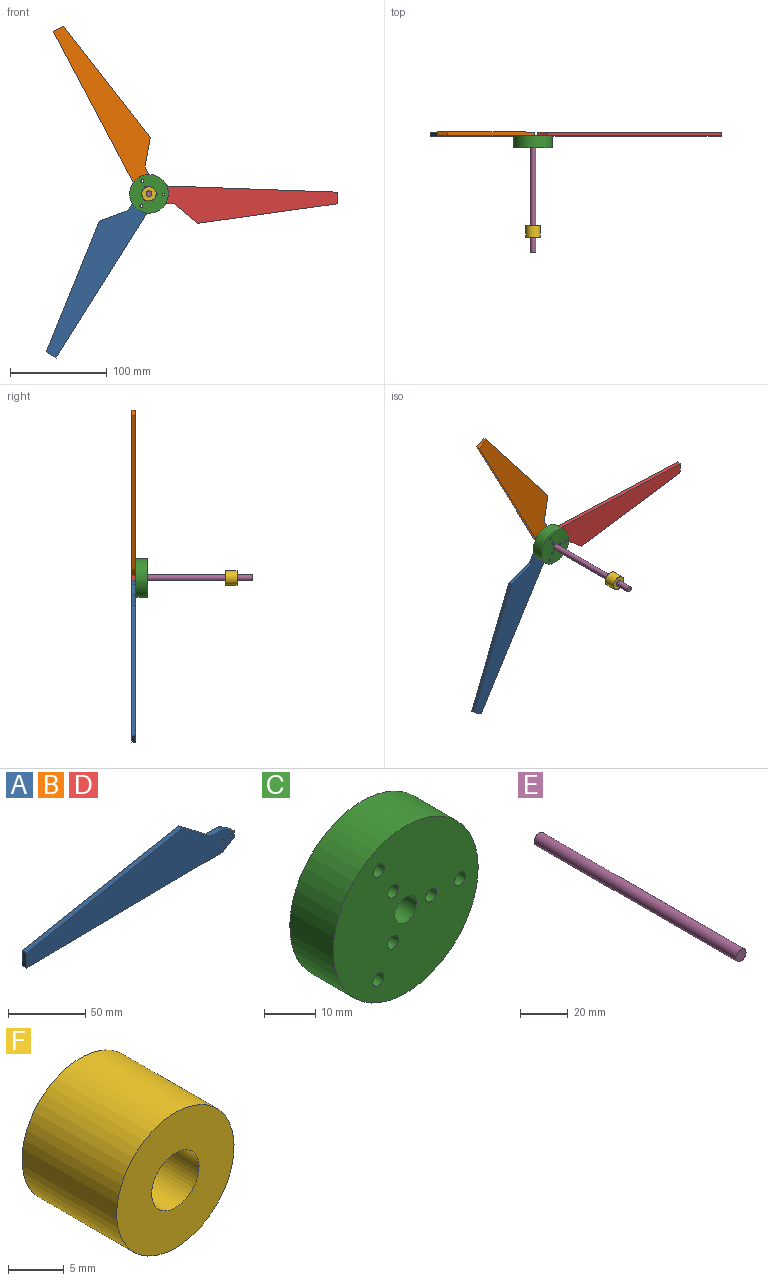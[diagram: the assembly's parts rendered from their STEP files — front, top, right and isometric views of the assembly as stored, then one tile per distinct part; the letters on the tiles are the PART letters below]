
ASSEMBLY  parts=6 mates=8
PART A: 12 faces, bbox 190x4x39.3 mm
  f0: plane 143x27.33mm, normal (-0.19,0,0.98), area 582.3mm2, adj f1,f7,f8,f9
  f1: plane 12x4mm, normal (-1,0,0), area 48mm2, adj f0,f2,f8,f9
  f2: plane 180x4mm, normal (0.01,0,-1), area 720.1mm2, adj f1,f3,f8,f9
  f3: plane 10x6.4mm, normal (0.54,0,-0.84), area 47.5mm2, adj f2,f4,f8,f9
  f4: plane 5.2x4mm, normal (1,0,0), area 20.8mm2, adj f3,f5,f8,f9
  f5: plane 10x6.4mm, normal (0.54,0,0.84), area 47.5mm2, adj f4,f6,f8,f9
  f6: plane 12x4mm, normal (0,0,1), area 48mm2, adj f5,f7,f8,f9
  f7: plane 25x19mm, normal (0.61,0,0.8), area 125.6mm2, adj f0,f6,f8,f9
  f8: plane 190x39.33mm, normal (0,-1,0), area 4551.9mm2, adj f0,f1,f2,f3,f4,f5,f6,f7
  f9: plane 190x39.33mm, normal (0,1,0), area 4551.9mm2, adj f0,f1,f2,f3,f4,f5,f6,f7
  f10: cylinder r=1.5mm len=4mm, axis (0,-1,0), area 37.7mm2, adj f8,f9
  f11: cylinder r=1.5mm len=4mm, axis (0,-1,0), area 37.7mm2, adj f8,f9
PART B: same geometry as A
PART C: 10 faces, bbox 40x12x40 mm
  f0: cylinder r=20mm len=40mm, axis (0,1,0), area 1508mm2, adj f1,f2
  f1: plane 40x40mm, normal (0,-1,0), area 1186mm2, adj f0,f3,f4,f5,f6,f7,f8,f9
  f2: plane 40x40mm, normal (0,1,0), area 1186mm2, adj f0,f3,f4,f5,f6,f7,f8,f9
  f3: cylinder r=3mm len=12mm, axis (0,-1,0), area 226.2mm2, adj f1,f2
  f4: cylinder r=1.5mm len=12mm, axis (0,-1,0), area 113.1mm2, adj f1,f2
  f5: cylinder r=1.5mm len=12mm, axis (0,-1,0), area 113.1mm2, adj f1,f2
  f6: cylinder r=1.5mm len=12mm, axis (0,-1,0), area 113.1mm2, adj f1,f2
  f7: cylinder r=1.5mm len=12mm, axis (0,-1,0), area 113.1mm2, adj f1,f2
  f8: cylinder r=1.5mm len=12mm, axis (0,-1,0), area 113.1mm2, adj f1,f2
  f9: cylinder r=1.5mm len=12mm, axis (0,-1,0), area 113.1mm2, adj f1,f2
PART D: same geometry as A
PART E: 3 faces, bbox 6x120x6 mm
  f0: cylinder r=3mm len=120mm, axis (0,1,0), area 2261.9mm2, adj f1,f2
  f1: plane 6x6mm, normal (0,-1,0), area 28.3mm2, adj f0
  f2: plane 6x6mm, normal (0,1,0), area 28.3mm2, adj f0
PART F: 4 faces, bbox 14.9x12x14.9 mm
  f0: cylinder r=3mm len=12mm, axis (0,1,0), area 226.2mm2, adj f2,f3
  f1: cylinder r=7.43mm len=14.86mm, axis (0,1,0), area 560.1mm2, adj f2,f3
  f2: plane 14.86x14.86mm, normal (0,-1,0), area 145.1mm2, adj f0,f1
  f3: plane 14.86x14.86mm, normal (0,1,0), area 145.1mm2, adj f0,f1
PLACE A rot(axis=(0,-1,0),57.2deg) t=(-99.57,44.41,-140.73)mm
PLACE B rot(axis=(0,1,0),62.8deg) t=(-84.35,44.41,138.42)mm
PLACE C rot(axis=(0,1,0),2.4deg) t=(-11.38,36.41,-5.55)mm fixed
PLACE D rot(axis=(0,-1,0),177.2deg) t=(149.79,44.41,-14.34)mm
PLACE E rot(axis=(0,1,0),2.4deg) t=(-11.38,42.41,-5.55)mm
PLACE F rot(axis=(0,1,0),2.4deg) t=(-11.38,-50.09,-5.55)mm
MATE revolute C.f5 <-> A.f11  axis (0,-1,0) through (-15.17,42.41,-11.44)mm
MATE revolute D.f11 <-> C.f4  axis (0,-1,0) through (-4.39,42.41,-5.9)mm
MATE fastened F.f0 <-> E.f0  axis (0,-1,0) through (-11.38,-62.09,-5.55)mm
MATE revolute D.f10 <-> C.f9  axis (0,-1,0) through (3.6,42.41,-6.3)mm
MATE revolute B.f10 <-> C.f7  axis (0,-1,0) through (-18.23,42.41,7.79)mm
MATE revolute A.f10 <-> C.f6  axis (0,-1,0) through (-19.51,42.41,-18.16)mm
MATE fastened C.f0 <-> E.f0  axis (0,1,0) through (-11.38,42.41,-5.55)mm
MATE revolute C.f8 <-> B.f11  axis (0,1,0) through (-14.57,42.41,0.67)mm
